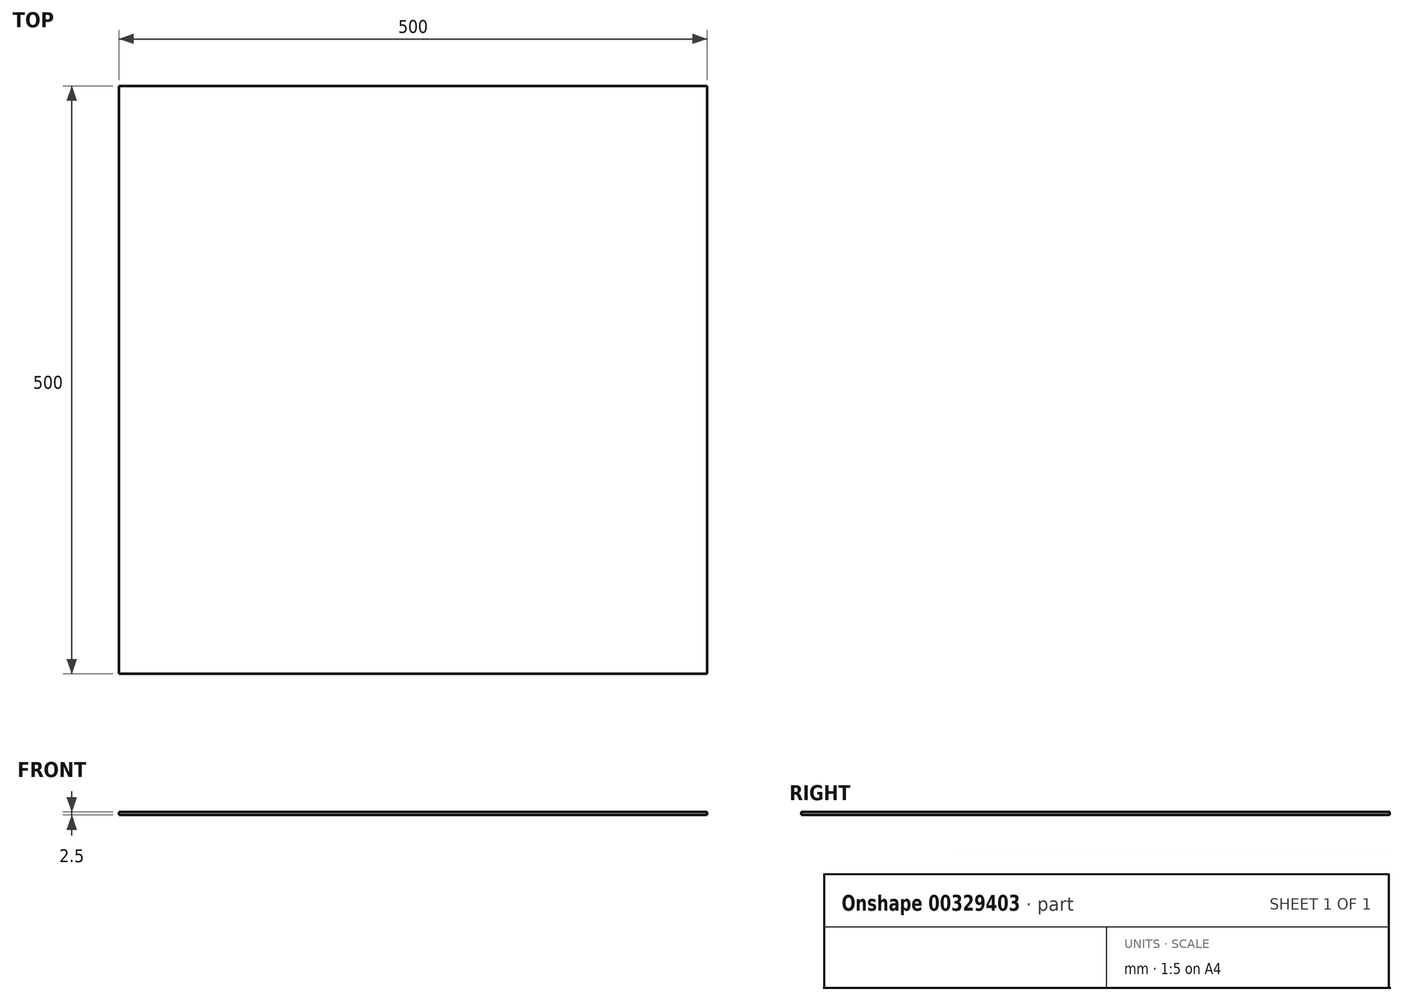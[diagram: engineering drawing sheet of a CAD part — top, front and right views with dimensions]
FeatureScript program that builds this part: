
annotation { "Feature Type Name" : "Feature", "Feature Type Description" : "" }
export const myFeature = defineFeature(function(context is Context, id is Id, definition is map)
    precondition{}
    {
        {
            var Q0;
            Q0=qCreatedBy(makeId("Top.planeOp"),FACE);
            var sketch = newSketch(context, id + "F0", { "sketchPlane" : qUnion([Q0])});
            skLineSegment(sketch, "E0.bottom", {"start": v(250, 250) * mm, "end": v(-250, 250) * mm});
            skLineSegment(sketch, "E0.top", {"start": v(250, -250) * mm, "end": v(-250, -250) * mm});
            skLineSegment(sketch, "E0.left", {"start": v(250, 250) * mm, "end": v(250, -250) * mm});
            skLineSegment(sketch, "E0.right", {"start": v(-250, 250) * mm, "end": v(-250, -250) * mm});
            skPoint(sketch, "E0.middle", {"position": v(0, 0) * mm});
            skSolve(sketch);
        }
        {
            var Q0;
            Q0=makeQuery(id+"F0.imprint","IMPRINT",FACE,{"disambiguationData":[TD([[makeQuery(id+"F0.imprint","IMPRINT",EDGE,{"derivedFrom":sQuery(id+"F0.wireOp",EDGE,"E0.bottom")}),1.0]])]});
            extrude(context, id + "F1", {"entities" : qUnion([Q0]), "depth" : 2.5 * mm});
        }
    });
